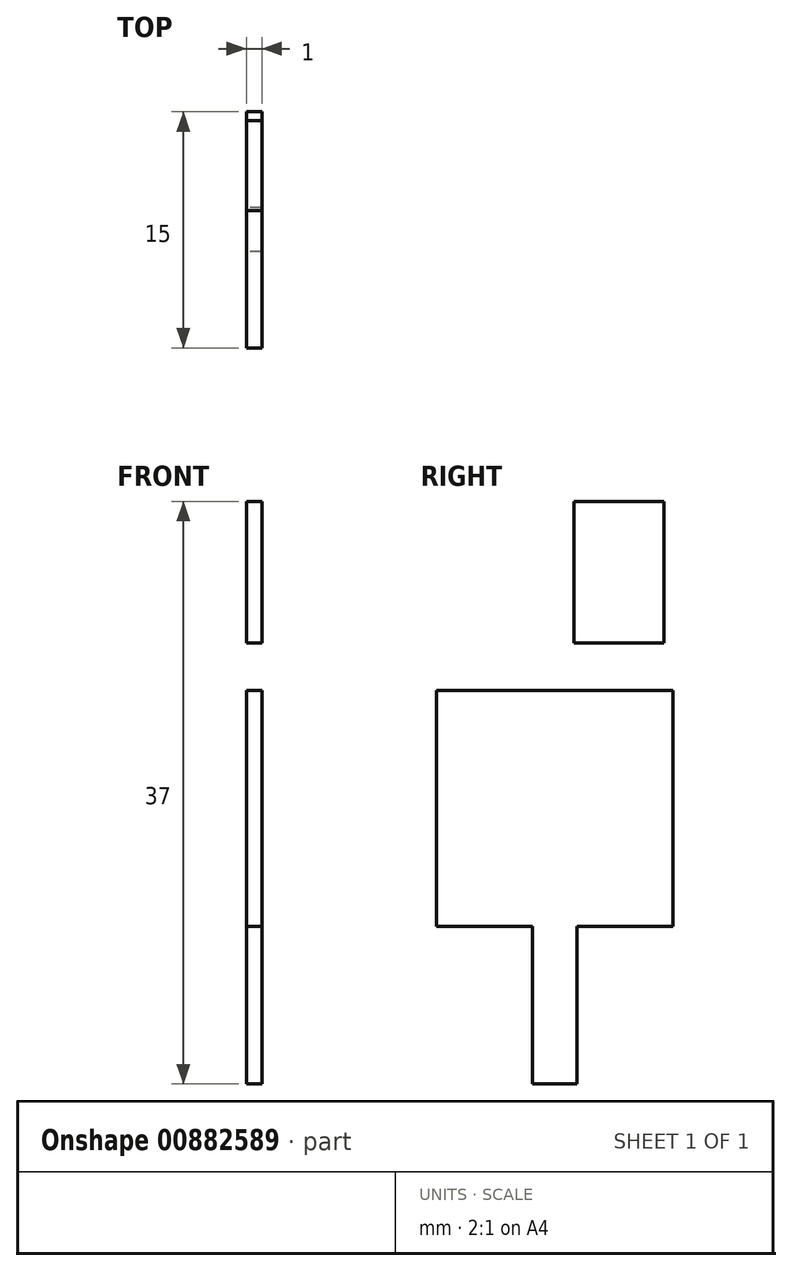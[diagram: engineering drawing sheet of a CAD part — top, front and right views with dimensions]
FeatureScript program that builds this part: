
annotation { "Feature Type Name" : "Feature", "Feature Type Description" : "" }
export const myFeature = defineFeature(function(context is Context, id is Id, definition is map)
    precondition{}
    {
        {
            var Q0;
            Q0=qCreatedBy(makeId("Right.planeOp"),FACE);
            var sketch = newSketch(context, id + "F0", { "sketchPlane" : qUnion([Q0])});
            skLineSegment(sketch, "E0.bottom", {"start": v(0, 0) * mm, "end": v(11.5, 0) * mm});
            skLineSegment(sketch, "E0.top", {"start": v(0, -15) * mm, "end": v(4.35, -15) * mm});
            skLineSegment(sketch, "E1", {"start": v(5.25, -25) * mm, "end": v(6.25, -25) * mm});
            skLineSegment(sketch, "E2.trimOffspring", {"start": v(7.15, -15) * mm, "end": v(11.5, -15) * mm});
            skLineSegment(sketch, "E3", {"start": v(11.5, 3) * mm, "end": v(8.25, 3) * mm});
            skLineSegment(sketch, "E4.0", {"start": v(-1.75, 0) * mm, "end": v(-1.75, -15) * mm});
            skLineSegment(sketch, "E5.0", {"start": v(13.25, 0) * mm, "end": v(13.25, -15) * mm});
            skLineSegment(sketch, "E6", {"start": v(-1.75, 0) * mm, "end": v(13.25, 0) * mm});
            skLineSegment(sketch, "E7", {"start": v(13.25, -15) * mm, "end": v(7.15, -15) * mm});
            skPoint(sketch, "E8.orphan", {"position": v(6.5, 18) * mm});
            skPoint(sketch, "E9.orphan", {"position": v(6.5, 3) * mm});
            skLineSegment(sketch, "E10", {"start": v(12.68, 3) * mm, "end": v(8.25, 3) * mm});
            skLineSegment(sketch, "E11.0", {"start": v(4.35, -15) * mm, "end": v(4.35, -25) * mm});
            skLineSegment(sketch, "E12.0", {"start": v(7.15, -15) * mm, "end": v(7.15, -25) * mm});
            skLineSegment(sketch, "E13", {"start": v(4.35, -25) * mm, "end": v(7.15, -25) * mm});
            skPoint(sketch, "E14.end.orphan", {"position": v(5.75, -25) * mm});
            skPoint(sketch, "E14.start.orphan", {"position": v(5.75, -15) * mm});
            skLineSegment(sketch, "E15.trimOffspring", {"start": v(4.35, -15) * mm, "end": v(-1.75, -15) * mm});
            skLineSegment(sketch, "E16", {"start": v(12.68, 12) * mm, "end": v(12.68, 3) * mm});
            skLineSegment(sketch, "E17", {"start": v(12.68, 3) * mm, "end": v(6.98, 3) * mm});
            skLineSegment(sketch, "E18", {"start": v(6.98, 3) * mm, "end": v(6.98, 12) * mm});
            skLineSegment(sketch, "E19.0", {"start": v(12.68, 12) * mm, "end": v(8.25, 12) * mm});
            skLineSegment(sketch, "E20.0", {"start": v(6.98, 12) * mm, "end": v(8.25, 12) * mm});
            skPoint(sketch, "E21.end.orphan", {"position": v(8.25, 18) * mm});
            skPoint(sketch, "E22.orphan", {"position": v(6.98, 18) * mm});
            skSolve(sketch);
        }
        {
            var Q0;
            Q0=makeQuery(id+"F0.imprint","IMPRINT",FACE,{"disambiguationData":[TD([[makeQuery(id+"F0.imprint","IMPRINT",EDGE,{"derivedFrom":sQuery(id+"F0.wireOp",EDGE,"E0.bottom")}),-1.0]])]});
            var Q1;
            Q1=makeQuery(id+"F0.imprint","IMPRINT",FACE,{"disambiguationData":[TD([[makeQuery(id+"F0.imprint","IMPRINT",EDGE,{"derivedFrom":sQuery(id+"F0.wireOp",EDGE,"E3")}),-1.0]])]});
            var Q2;
            {var subQ3=sQuery(id+"F0.wireOp",EDGE,"63f1d356-c40f-4f39-ade3-4e022c9102be.0");Q2=makeQuery(id+"F0.imprint","IMPRINT",FACE,{"disambiguationData":[TD([[makeQuery(id+"F0.imprint","IMPRINT",EDGE,{"derivedFrom":subQ3}),1.0]])]});}
            var Q3;
            {var subQ1=sQuery(id+"F0.wireOp",EDGE,"E0.bottom");Q3=makeQuery(id+"F0.imprint","IMPRINT",FACE,{"disambiguationData":[TD([[makeQuery(id+"F0.imprint","IMPRINT",EDGE,{"derivedFrom":subQ1}),-1.0]])]});}
            var Q4;
            {var subQ0=sQuery(id+"F0.wireOp",EDGE,"5dc07093-3f57-4306-a93b-4e72212c7467.0");Q4=makeQuery(id+"F0.imprint","IMPRINT",FACE,{"disambiguationData":[TD([[makeQuery(id+"F0.imprint","IMPRINT",EDGE,{"derivedFrom":subQ0}),1.0]])]});}
            var Q5;
            Q5=makeQuery(id+"F0.imprint","IMPRINT",FACE,{"disambiguationData":[TD([[makeQuery(id+"F0.imprint","IMPRINT",EDGE,{"derivedFrom":sQuery(id+"F0.wireOp",EDGE,"E3")}),-1.0]])]});
            extrude(context, id + "F1", {"entities" : qUnion([Q0, Q1, Q2, Q3, Q4, Q5]), "depth" : 1 * mm, "offsetDistance" : 25 * mm});
        }
    });
